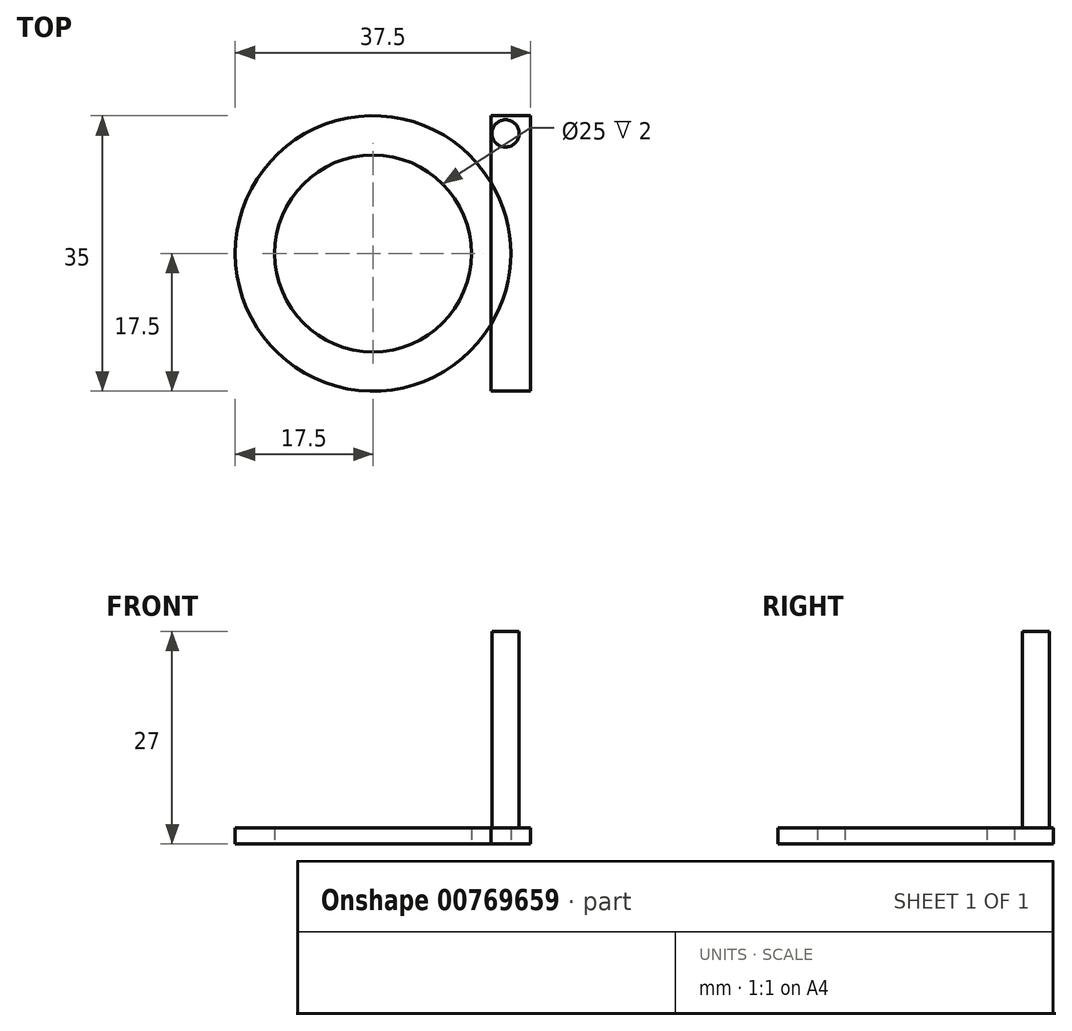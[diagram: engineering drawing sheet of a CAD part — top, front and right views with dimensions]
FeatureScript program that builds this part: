
annotation { "Feature Type Name" : "Feature", "Feature Type Description" : "" }
export const myFeature = defineFeature(function(context is Context, id is Id, definition is map)
    precondition{}
    {
        {
            var Q0;
            Q0=qCreatedBy(makeId("Top.planeOp"),FACE);
            var sketch = newSketch(context, id + "F0", { "sketchPlane" : qUnion([Q0])});
            skCircle(sketch, "E0", {"center": v(0, 0) * mm, "radius": 17.5 * mm});
            skCircle(sketch, "E1", {"center": v(0, 0) * mm, "radius": 12.5 * mm});
            skLineSegment(sketch, "E2.bottom", {"start": v(15, 17.5) * mm, "end": v(20, 17.5) * mm});
            skLineSegment(sketch, "E2.top", {"start": v(15, -17.5) * mm, "end": v(20, -17.5) * mm});
            skLineSegment(sketch, "E2.left", {"start": v(15, 17.5) * mm, "end": v(15, -17.5) * mm});
            skLineSegment(sketch, "E2.right", {"start": v(20, 17.5) * mm, "end": v(20, -17.5) * mm});
            skSolve(sketch);
        }
        {
            var Q0;
            Q0=makeQuery(id+"F0.imprint","IMPRINT",FACE,{"disambiguationData":[TD([[makeQuery(id+"F0.imprint","IMPRINT",EDGE,{"derivedFrom":sQuery(id+"F0.wireOp",EDGE,"E1")}),-1.0]])]});
            var Q1;
            {var subQ0=sQuery(id+"F0.wireOp",EDGE,"E2.left");var subQ1=sQuery(id+"F0.wireOp",EDGE,"E0");var subQ2=makeQuery(id+"F0.imprint","INTERSECT",VERTEX,{"disambiguationData":[OD(0.0)],"derivedFrom":[subQ1,subQ0]});Q1=makeQuery(id+"F0.imprint","IMPRINT",FACE,{"disambiguationData":[TD([[makeQuery(id+"F0.imprint","IMPRINT",EDGE,{"disambiguationData":[TD([[subQ2,1.0]])],"derivedFrom":subQ1}),1.0]])]});}
            var Q2;
            {var subQ1=sQuery(id+"F0.wireOp",EDGE,"E2.bottom");Q2=makeQuery(id+"F0.imprint","IMPRINT",FACE,{"disambiguationData":[TD([[makeQuery(id+"F0.imprint","IMPRINT",EDGE,{"derivedFrom":subQ1}),-1.0]])]});}
            extrude(context, id + "F1", {"entities" : qUnion([Q0, Q1, Q2]), "depth" : 2 * mm, "offsetDistance" : 25 * mm});
        }
        {
            var Q0;
            Q0=makeQuery(id+"F1.opExtrude","CAP_FACE",FACE,{"disambiguationData":[OSD([sQuery(id+"F0.wireOp",EDGE,"E0"),sQuery(id+"F0.wireOp",EDGE,"E1"),sQuery(id+"F0.wireOp",EDGE,"E2.bottom"),sQuery(id+"F0.wireOp",EDGE,"E2.top"),sQuery(id+"F0.wireOp",EDGE,"E2.left"),sQuery(id+"F0.wireOp",EDGE,"E2.right")])],"isStart":false});
            var sketch = newSketch(context, id + "F2", { "sketchPlane" : qUnion([Q0])});
            skCircle(sketch, "E3", {"center": v(16.83, 15.25) * mm, "radius": 1.73 * mm});
            skSolve(sketch);
        }
        {
            var Q0;
            Q0=makeQuery(id+"F2.imprint","IMPRINT",FACE,{"disambiguationData":[TD([[makeQuery(id+"F2.imprint","IMPRINT",EDGE,{"derivedFrom":sQuery(id+"F2.wireOp",EDGE,"E3")}),1.0]])]});
            extrude(context, id + "F3", {"entities" : qUnion([Q0]), "operationType" : NewBodyOperationType.ADD, "depth" : 25 * mm, "offsetDistance" : 25 * mm});
        }
    });
